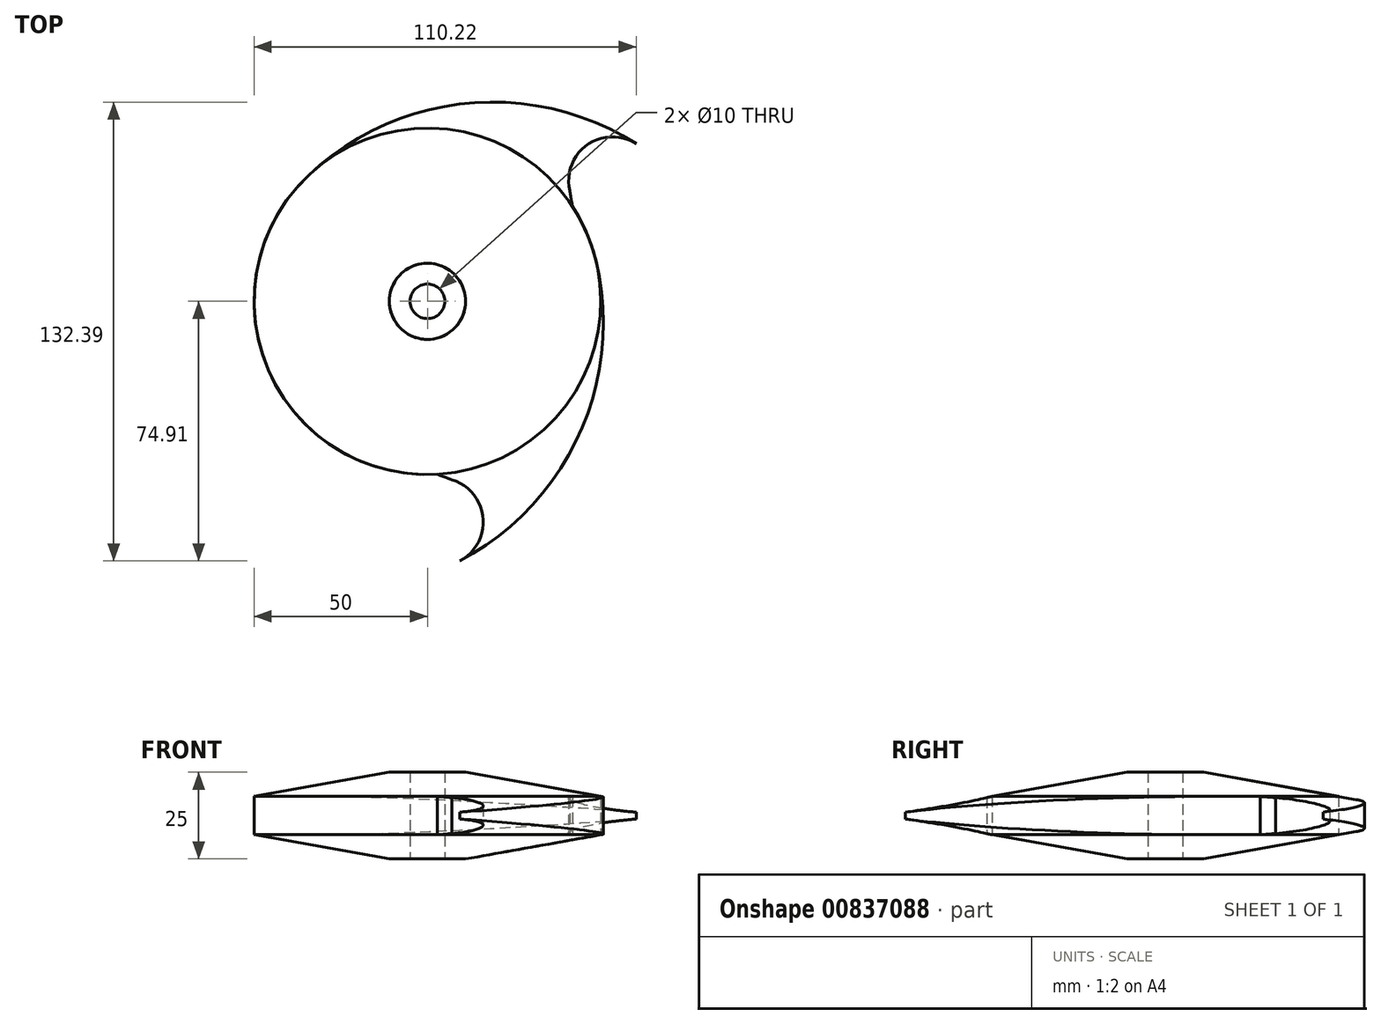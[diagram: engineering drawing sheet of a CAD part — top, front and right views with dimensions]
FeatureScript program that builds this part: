
annotation { "Feature Type Name" : "Feature", "Feature Type Description" : "" }
export const myFeature = defineFeature(function(context is Context, id is Id, definition is map)
    precondition{}
    {
        {
            var Q0;
            Q0=qCreatedBy(makeId("Top.planeOp"),FACE);
            var sketch = newSketch(context, id + "F0", { "sketchPlane" : qUnion([Q0])});
            skCircle(sketch, "E0", {"center": v(0, 0) * mm, "radius": 50 * mm});
            skCircle(sketch, "E1", {"center": v(0, 0) * mm, "radius": 27.5 * mm});
            skArc(sketch, "E2", {"start": v(-69.53, 29.4) * mm, "mid": v(-55.17, -18.68) * mm, "end": v(-14.39, -47.88) * mm});
            skLineSegment(sketch, "E3", {"start": v(-44.57, 22.66) * mm, "end": v(-45.5, 23.13) * mm});
            skPoint(sketch, "E4", {"position": v(-56.83, 28.9) * mm});
            skArc(sketch, "E5", {"start": v(-69.53, 29.4) * mm, "mid": v(-60.03, 16.6) * mm, "end": v(-45.5, 23.13) * mm});
            skPoint(sketch, "E6.trimOffspring.end.orphan", {"position": v(-69.09, 35.12) * mm});
            skCircle(sketch, "E7", {"center": v(0, 0) * mm, "radius": 5 * mm});
            skLineSegment(sketch, "E8", {"start": v(3.13, -3.9) * mm, "end": v(3.13, 3.9) * mm});
            skSolve(sketch);
        }
        {
            var Q0;
            {var subQ0=sQuery(id+"F0.wireOp",EDGE,"E2");Q0=makeQuery(id+"F0.imprint","IMPRINT",FACE,{"disambiguationData":[TD([[makeQuery(id+"F0.imprint","IMPRINT",EDGE,{"derivedFrom":subQ0}),1.0]])]});}
            var Q1;
            Q1=makeQuery(id+"F0.imprint","IMPRINT",FACE,{"disambiguationData":[TD([[makeQuery(id+"F0.imprint","IMPRINT",EDGE,{"derivedFrom":sQuery(id+"F0.wireOp",EDGE,"E1")}),-1.0]])]});
            var Q2;
            Q2=makeQuery(id+"F0.imprint","IMPRINT",FACE,{"disambiguationData":[TD([[makeQuery(id+"F0.imprint","IMPRINT",EDGE,{"derivedFrom":sQuery(id+"F0.wireOp",EDGE,"E1")}),1.0]])]});
            var Q3;
            {var subQ0=sQuery(id+"F0.wireOp",EDGE,"E8");Q3=makeQuery(id+"F0.imprint","IMPRINT",FACE,{"disambiguationData":[TD([[makeQuery(id+"F0.imprint","IMPRINT",EDGE,{"derivedFrom":subQ0}),-1.0]])]});}
            extrude(context, id + "F1", {"entities" : qUnion([Q0, Q1, Q2, Q3]), "depth" : 25 * mm, "offsetDistance" : 25 * mm});
        }
        {
            var Q0;
            Q0=qCreatedBy(makeId("Front.planeOp"),FACE);
            var sketch = newSketch(context, id + "F2", { "sketchPlane" : qUnion([Q0])});
            skLineSegment(sketch, "E9", {"start": v(0, 0) * mm, "end": v(0, 42.37) * mm});
            skSolve(sketch);
        }
        {
            var Q0;
            Q0=makeQuery(id+"F1.opExtrude","SWEPT_EDGE",EDGE,{"disambiguationData":[OSD([sQuery(id+"F0.wireOp",EDGE,"E3"),sQuery(id+"F0.wireOp",EDGE,"E5")])]});
            chamfer(context, id + "F3", {"entities" : qUnion([Q0]), "chamferType" : ChamferType.TWO_OFFSETS, "width1" : 5 * mm, "oppositeDirection" : false, "width2" : 2 * mm, "tangentPropagation" : true});
        }
        {
            var Q0;
            Q0=makeQuery(id+"F1.opExtrude","SWEPT_BODY",BODY,{"disambiguationData":[OSD([sQuery(id+"F0.wireOp",EDGE,"E0"),sQuery(id+"F0.wireOp",EDGE,"E2"),sQuery(id+"F0.wireOp",EDGE,"E3"),sQuery(id+"F0.wireOp",EDGE,"E5"),sQuery(id+"F0.wireOp",EDGE,"E7")])]});
            var Q1;
            Q1=sQuery(id+"F2.wireOp",EDGE,"E9");
            circularPattern(context, id + "F4", {"entities" : qUnion([Q0]), "axis" : qUnion([Q1]), "angle" : 360 * degree, "instanceCount" : 3, "equalSpace" : true});
        }
        {
            var Q0;
            Q0=qCreatedBy(makeId("Front.planeOp"),FACE);
            var sketch = newSketch(context, id + "F5", { "sketchPlane" : qUnion([Q0])});
            skPoint(sketch, "E10.start.orphan", {"position": v(0, 7.03) * mm});
            skLineSegment(sketch, "E11", {"start": v(-11, 0) * mm, "end": v(-81, 0) * mm});
            skLineSegment(sketch, "E12", {"start": v(-81, 0) * mm, "end": v(-81, 12.5) * mm});
            skLineSegment(sketch, "E13", {"start": v(-81, 12.5) * mm, "end": v(-11, 0) * mm});
            skLineSegment(sketch, "E14", {"start": v(-81, 12.5) * mm, "end": v(-81, 25) * mm});
            skLineSegment(sketch, "E15", {"start": v(-81, 25) * mm, "end": v(0, 25) * mm});
            skLineSegment(sketch, "E16", {"start": v(-11, 0) * mm, "end": v(-11, 25) * mm});
            skLineSegment(sketch, "E17", {"start": v(-11, 25) * mm, "end": v(-81, 12.5) * mm});
            skSolve(sketch);
        }
        {
            var Q0;
            Q0=makeQuery(id+"F5.imprint","IMPRINT",FACE,{"disambiguationData":[TD([[makeQuery(id+"F5.imprint","IMPRINT",EDGE,{"derivedFrom":sQuery(id+"F5.wireOp",EDGE,"E11")}),-1.0]])]});
            var Q1;
            {var subQ0=sQuery(id+"F5.wireOp",EDGE,"E14");Q1=makeQuery(id+"F5.imprint","IMPRINT",FACE,{"disambiguationData":[TD([[makeQuery(id+"F5.imprint","IMPRINT",EDGE,{"derivedFrom":subQ0}),-1.0]])]});}
            var Q2;
            Q2=sQuery(id+"F2.wireOp",EDGE,"E9");
            revolve(context, id + "F6", {"operationType" : NewBodyOperationType.REMOVE, "surfaceOperationType" : NewSurfaceOperationType.NEW, "entities" : qUnion([Q0, Q1]), "axis" : qUnion([Q2]), "revolveType" : RevolveType.FULL, "oppositeDirection" : true});
        }
        {
            var Q0;
            {var subQ0=sQuery(id+"F0.wireOp",EDGE,"E8");Q0=makeQuery(id+"F0.imprint","IMPRINT",FACE,{"disambiguationData":[TD([[makeQuery(id+"F0.imprint","IMPRINT",EDGE,{"derivedFrom":subQ0}),1.0]])]});}
            extrude(context, id + "F7", {"entities" : qUnion([Q0]), "operationType" : NewBodyOperationType.REMOVE, "depth" : 25 * mm, "offsetDistance" : 25 * mm});
        }
    });
